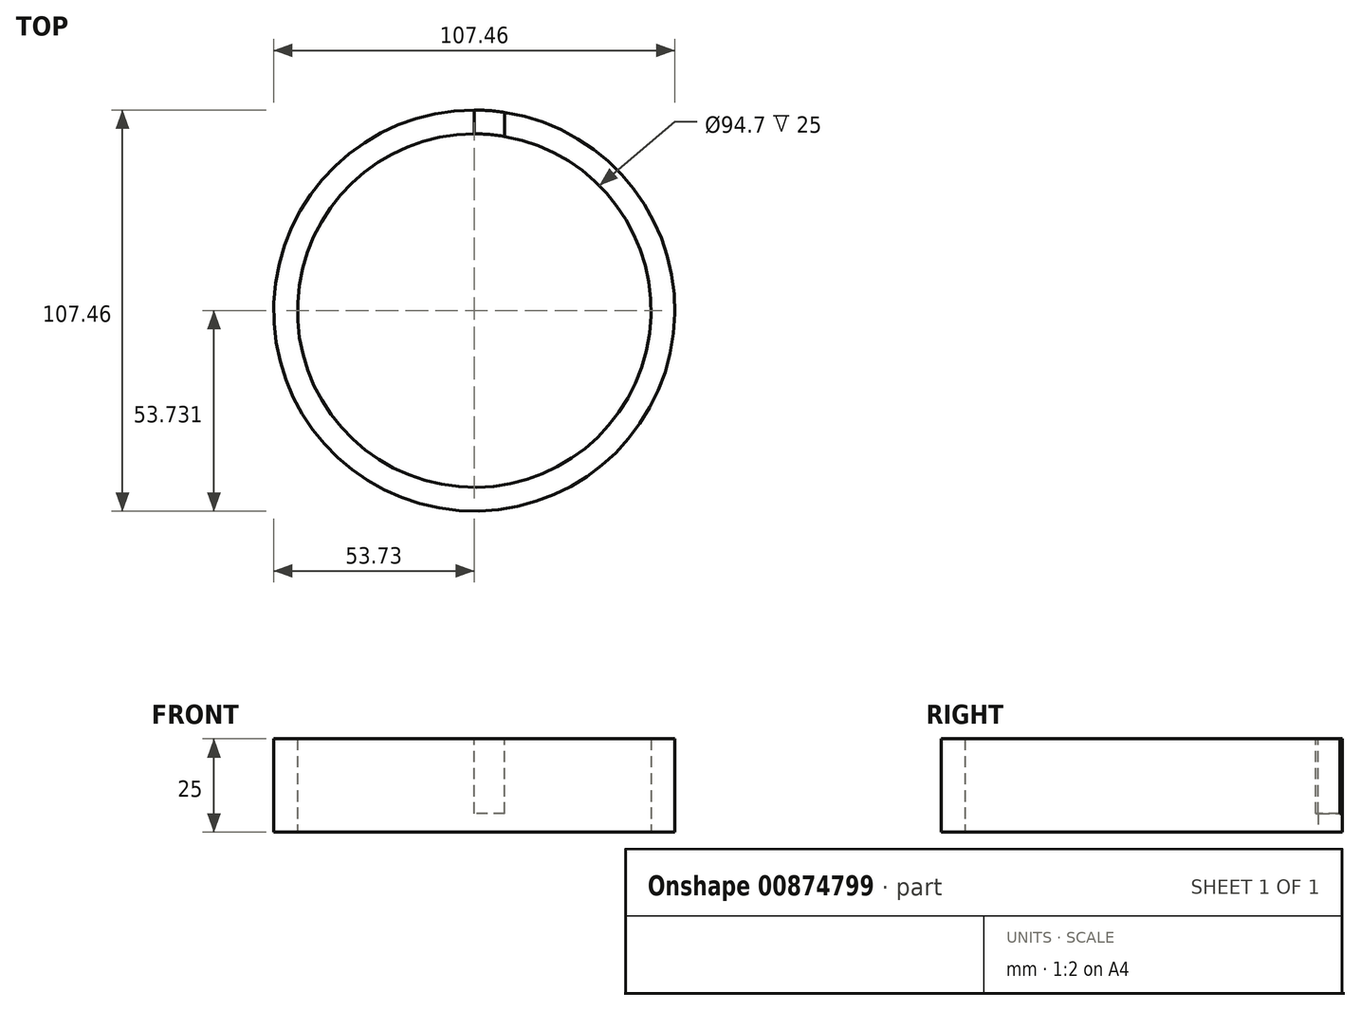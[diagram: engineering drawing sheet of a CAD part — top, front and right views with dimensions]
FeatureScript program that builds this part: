
annotation { "Feature Type Name" : "Feature", "Feature Type Description" : "" }
export const myFeature = defineFeature(function(context is Context, id is Id, definition is map)
    precondition{}
    {
        {
            var Q0;
            Q0=qCreatedBy(makeId("Top.planeOp"),FACE);
            var sketch = newSketch(context, id + "F0", { "sketchPlane" : qUnion([Q0])});
            skCircle(sketch, "E0", {"center": v(0, 17.1) * mm, "radius": 53.73 * mm});
            skCircle(sketch, "E1", {"center": v(0, 17.1) * mm, "radius": 47.35 * mm});
            skSolve(sketch);
        }
        {
            var Q0;
            Q0=makeQuery(id+"F0.imprint","IMPRINT",FACE,{"disambiguationData":[TD([[makeQuery(id+"F0.imprint","IMPRINT",EDGE,{"derivedFrom":sQuery(id+"F0.wireOp",EDGE,"E0")}),1.0]])]});
            extrude(context, id + "F1", {"entities" : qUnion([Q0]), "depth" : 25 * mm, "offsetDistance" : 25 * mm});
        }
        {
            var Q0;
            Q0=makeQuery(id+"F1.opExtrude","CAP_FACE",FACE,{"disambiguationData":[OSD([sQuery(id+"F0.wireOp",EDGE,"E0"),sQuery(id+"F0.wireOp",EDGE,"E1")])],"isStart":false});
            var sketch = newSketch(context, id + "F2", { "sketchPlane" : qUnion([Q0])});
            skLineSegment(sketch, "E2", {"start": v(0, 64.45) * mm, "end": v(0, 70.83) * mm});
            skLineSegment(sketch, "E3", {"start": v(0, 70.83) * mm, "end": v(8.18, 70.83) * mm});
            skLineSegment(sketch, "E4", {"start": v(8.18, 70.83) * mm, "end": v(8.18, 63.74) * mm});
            skLineSegment(sketch, "E5", {"start": v(8.18, 63.74) * mm, "end": v(0, 64.45) * mm});
            skSolve(sketch);
        }
        {
            var Q0;
            {var subQ0=sQuery(id+"F2.wireOp",EDGE,"E2");Q0=makeQuery(id+"F2.imprint","IMPRINT",FACE,{"disambiguationData":[TD([[makeQuery(id+"F2.imprint","IMPRINT",EDGE,{"derivedFrom":subQ0}),-1.0]])]});}
            extrude(context, id + "F3", {"entities" : qUnion([Q0]), "operationType" : NewBodyOperationType.REMOVE, "oppositeDirection" : true, "depth" : 20 * mm, "offsetDistance" : 25 * mm});
        }
    });
